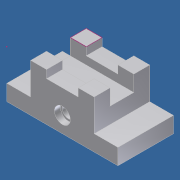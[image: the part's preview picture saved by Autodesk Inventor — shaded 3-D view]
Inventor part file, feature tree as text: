
AUTODESK INVENTOR PART (.ipt)
format: ipt  version: unknown  size: 210,944 bytes
history: native  units: in
note: dims shown in document units (in); Inventor stores cm internally (conversion verified against a paired STEP export)
features: sketch x4, extrude x2, hole x1
ambient origin geometry x8: Origin, YZ Plane, XZ Plane, XY Plane, X Axis, Y Axis, Z Axis, Center Point
bodies: Solid1 (feature_tree)
feature tree (7):
  extrude  "Extrusion1"  Depth=1.0in
  extrude  "Extrusion2"  Depth=1.0in
  hole  "Hole1"  [1 undecoded]
  sketch  "Sketch4"  dims[d6=0.5in d7=1.0in d8=2.0in d9=1.0in d10=1.5in d11=1.5in d12=3.5in d13=0.0in d14=1.0in d15=1.0in d16=1.5in d17=1.0in d18=7.0in d19=0.0in d20=1.0in d21=3.5in d22=0.75in d23=0.75in d24=1.0in d25=0.375in d26=0.5635in d27=1.5in d28=0.8108in]
  sketch  "Sketch1"  dims[d0=7.0in d1=1.0in]
  sketch  "Sketch2"  dims[d2=2.0in d3=1.0in]
  sketch  "Sketch3"  dims[d4=2.0in d5=0.5in]
note: 1 required parameter value undecoded (feature->parameter linkage not recoverable at this tier; creation-order binding heuristic only, values carry confidence <= 0.55)
